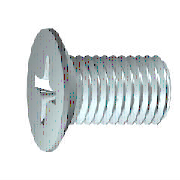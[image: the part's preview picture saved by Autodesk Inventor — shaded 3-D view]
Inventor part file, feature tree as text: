
AUTODESK INVENTOR PART (.ipt)
format: ipt  version: 2022 (Build 260153000, 153)  size: 230,912 bytes
history: native  units: mm (DEFAULTED — no unit token found)
features: sketch x1, other x1, extrude x1, plane x1
ambient origin geometry x7: Origin, YZ Plane, XZ Plane, X Axis, Y Axis, Z Axis, Center Point
bodies: Solid1 (feature_tree)
feature tree (4):
  sketch  "Эскиз1"
  other  "Базовый элемент"
  extrude  "Паз"  Depth=10.0mm
  plane  "Work Plane2"
